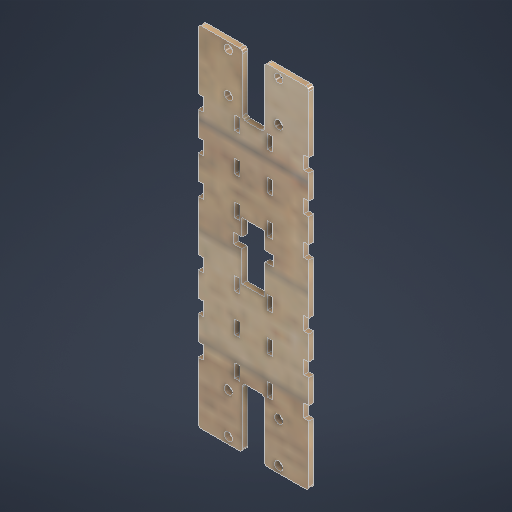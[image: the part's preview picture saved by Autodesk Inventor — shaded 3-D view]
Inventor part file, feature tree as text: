
AUTODESK INVENTOR PART (.ipt)
format: ipt  version: 2025.3 (Build 293356030, 356C)  size: 461,312 bytes
history: native  units: mm
features: other x2, sketch x2, extrude x1
ambient origin geometry x8: Origin, YZ Plane, XZ Plane, XY Plane, X Axis, Y Axis, Z Axis, Center Point
bodies: Body1 (feature_tree)
feature tree (5):
  other  "實體1"
  extrude  "擠出1"  Depth=66.0mm
  sketch  "草圖3"
  sketch  "草圖1"
  other  "草圖 - 矩形陣列1"
